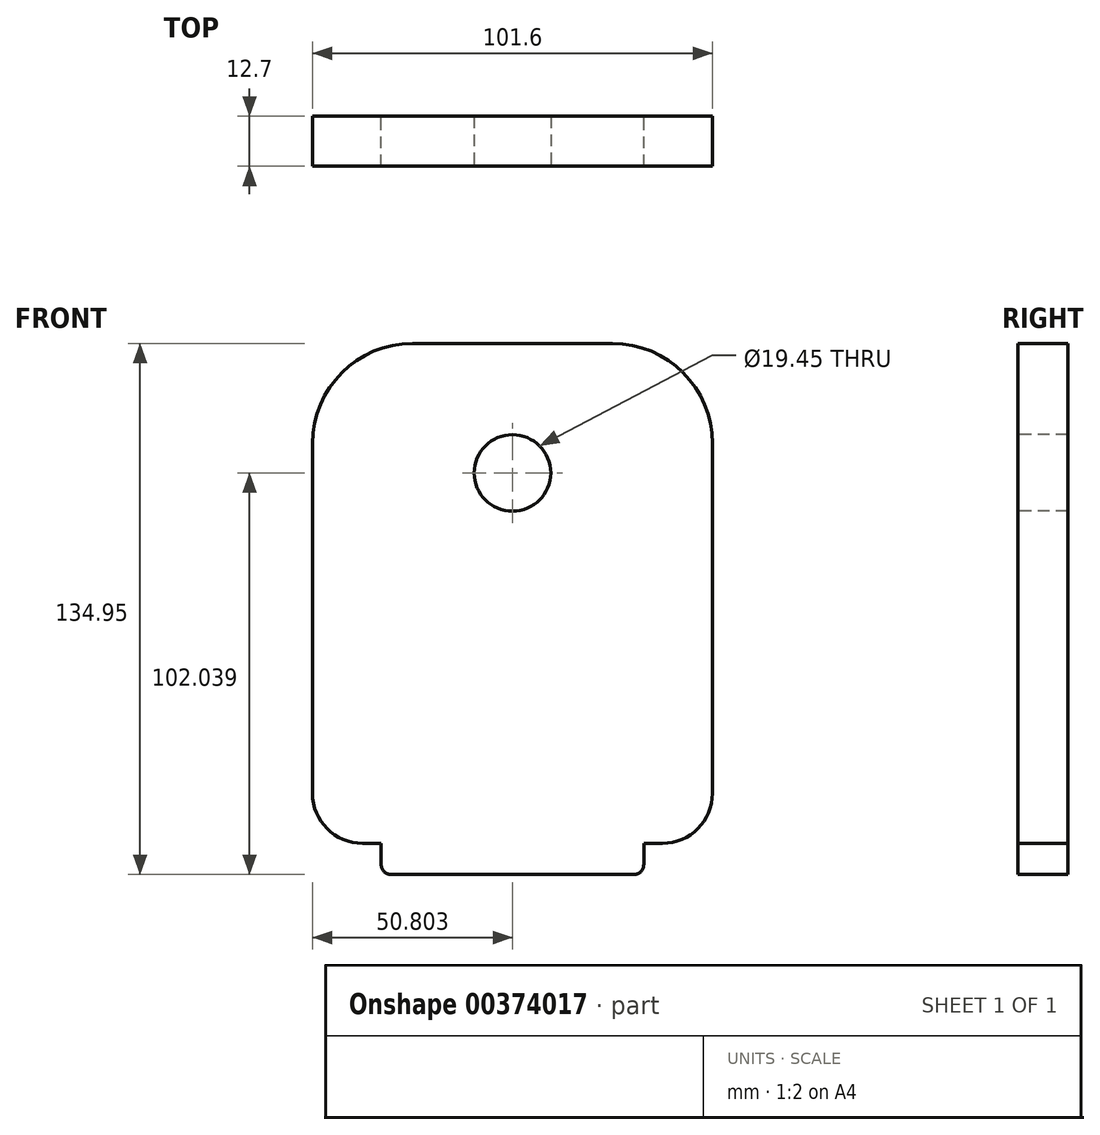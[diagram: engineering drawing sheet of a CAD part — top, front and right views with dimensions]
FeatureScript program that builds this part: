
annotation { "Feature Type Name" : "Feature", "Feature Type Description" : "" }
export const myFeature = defineFeature(function(context is Context, id is Id, definition is map)
    precondition{}
    {
        {
            var Q0;
            Q0=qCreatedBy(makeId("Front.planeOp"),FACE);
            var sketch = newSketch(context, id + "F0", { "sketchPlane" : qUnion([Q0])});
            skLineSegment(sketch, "E0", {"start": v(-59.75, 65.13) * mm, "end": v(-8.95, 65.13) * mm});
            skLineSegment(sketch, "E1", {"start": v(16.45, 39.73) * mm, "end": v(16.45, -49.17) * mm});
            skLineSegment(sketch, "E2", {"start": v(-85.15, -49.17) * mm, "end": v(-85.15, 39.73) * mm});
            skPoint(sketch, "E3.visualSharp", {"position": v(-85.15, 65.13) * mm});
            skArc(sketch, "E3.filletArc", {"start": v(-59.75, 65.13) * mm, "mid": v(-77.7, 57.69) * mm, "end": v(-85.15, 39.73) * mm});
            skPoint(sketch, "E4.visualSharp", {"position": v(16.45, 65.13) * mm});
            skArc(sketch, "E4.filletArc", {"start": v(16.45, 39.73) * mm, "mid": v(9.01, 57.69) * mm, "end": v(-8.95, 65.13) * mm});
            skPoint(sketch, "E5.visualSharp", {"position": v(16.45, -61.87) * mm});
            skPoint(sketch, "E6.visualSharp", {"position": v(-85.15, -61.87) * mm});
            skLineSegment(sketch, "E7", {"start": v(-72.45, -61.87) * mm, "end": v(-67.7, -61.87) * mm});
            skArc(sketch, "E8.filletArc", {"start": v(3.75, -61.87) * mm, "mid": v(12.73, -58.15) * mm, "end": v(16.45, -49.17) * mm});
            skArc(sketch, "E9.filletArc", {"start": v(-85.15, -49.17) * mm, "mid": v(-81.43, -58.15) * mm, "end": v(-72.45, -61.87) * mm});
            skPoint(sketch, "E10", {"position": v(-34.35, 32.22) * mm});
            skLineSegment(sketch, "E11.bottom", {"start": v(-3.54, -69.82) * mm, "end": v(-65.16, -69.82) * mm});
            skLineSegment(sketch, "E11.left", {"start": v(-1, -67.28) * mm, "end": v(-1, -61.87) * mm});
            skLineSegment(sketch, "E11.right", {"start": v(-67.7, -67.28) * mm, "end": v(-67.7, -61.87) * mm});
            skPoint(sketch, "E11.middle", {"position": v(-34.35, -61.87) * mm});
            skPoint(sketch, "E12.orphan", {"position": v(-1, -53.92) * mm});
            skPoint(sketch, "E13.orphan", {"position": v(-67.7, -53.92) * mm});
            skLineSegment(sketch, "E14.trimOffspring", {"start": v(-1, -61.87) * mm, "end": v(3.75, -61.87) * mm});
            skPoint(sketch, "E15.visualSharp", {"position": v(-1, -69.82) * mm});
            skArc(sketch, "E15.filletArc", {"start": v(-3.54, -69.82) * mm, "mid": v(-1.74, -69.08) * mm, "end": v(-1, -67.28) * mm});
            skPoint(sketch, "E16.visualSharp", {"position": v(-67.7, -69.82) * mm});
            skArc(sketch, "E16.filletArc", {"start": v(-67.7, -67.28) * mm, "mid": v(-66.95, -69.08) * mm, "end": v(-65.16, -69.82) * mm});
            skSolve(sketch);
        }
        {
            var Q0;
            Q0 = qSketchRegion(id + "F0", true);
            extrude(context, id + "F1", {"entities" : qUnion([Q0]), "depth" : 12.7 * mm, "offsetDistance" : 25 * mm});
        }
        {
            var Q0;
            Q0=sQuery(id+"F0.wireOp",VERTEX,"E10");
            var Q1;
            Q1=makeQuery(id+"F1.opExtrude","SWEPT_BODY",BODY,{"disambiguationData":[OSD([sQuery(id+"F0.wireOp",EDGE,"E0"),sQuery(id+"F0.wireOp",EDGE,"E1"),sQuery(id+"F0.wireOp",EDGE,"E2"),sQuery(id+"F0.wireOp",EDGE,"E3.filletArc"),sQuery(id+"F0.wireOp",EDGE,"E4.filletArc"),sQuery(id+"F0.wireOp",EDGE,"E7"),sQuery(id+"F0.wireOp",EDGE,"E8.filletArc"),sQuery(id+"F0.wireOp",EDGE,"E9.filletArc")])]});
            hole(context, id + "F2", {"style" : HoleStyle.SIMPLE, "endStyle" : HoleEndStyle.THROUGH, "oppositeDirection" : true, "standardTappedOrClearance" : lookupTablePath({ "fit" : "Close", "standard" : "ANSI", "size" : "3/4", "type" : "Clearance" }), "standardBlindInLast" : lookupTablePath({ "fit" : "Close", "standard" : "ANSI", "engagement" : "75%", "pitch" : "10 tpi", "size" : "3/4", "type" : "Clearance & tapped" }), "holeDiameter" : 19.45 * mm, "majorDiameter" : 5 * mm, "isTappedThrough" : true, "tappedDepth" : 50.8 * mm, "tapClearance" : 3, "locations" : qUnion([Q0]), "scope" : qUnion([Q1]), "startStyle" : HoleStartStyle.SKETCH});
        }
    });
